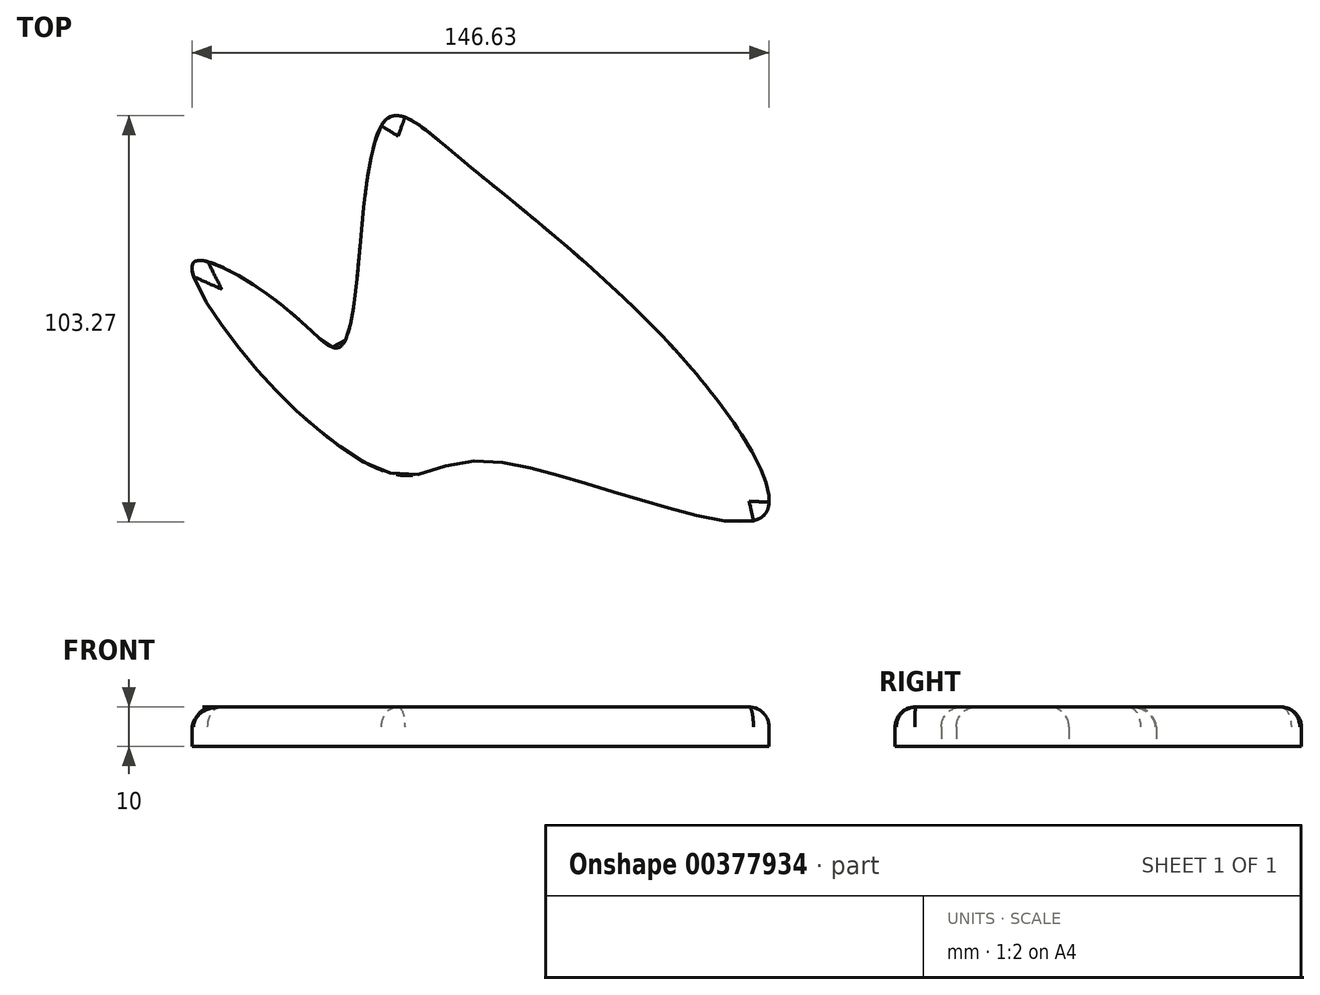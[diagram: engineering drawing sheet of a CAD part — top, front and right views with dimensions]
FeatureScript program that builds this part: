
annotation { "Feature Type Name" : "Feature", "Feature Type Description" : "" }
export const myFeature = defineFeature(function(context is Context, id is Id, definition is map)
    precondition{}
    {
        {
            var Q0;
            Q0=qCreatedBy(makeId("Top.planeOp"),FACE);
            var sketch = newSketch(context, id + "F0", { "sketchPlane" : qUnion([Q0])});
            skLineSegment(sketch, "E0", {"start": v(-136, -27.39) * mm, "end": v(-77.54, -6.3) * mm});
            skLineSegment(sketch, "E1", {"start": v(-118.9, 35.2) * mm, "end": v(-94.52, 0) * mm});
            skLineSegment(sketch, "E2", {"start": v(-77.54, -6.3) * mm, "end": v(-94.52, 0) * mm});
            skFitSpline(sketch, "E3", {"points": [v(126.55, -27.39) * mm, v(65.61, 27.87) * mm, v(47.85, 35.2) * mm, v(37.86, -20.84) * mm, v(25.14, -13.42) * mm, v(0, 0) * mm, v(15.93, -27.39) * mm, v(52.96, -54.3) * mm, v(74, -50.57) * mm, v(143.6, -65.21) * mm, v(126.55, -27.39) * mm]});
            skSolve(sketch);
        }
        {
            var Q0;
            Q0=makeQuery(id+"F0.imprint","IMPRINT",FACE,{"disambiguationData":[TD([[makeQuery(id+"F0.imprint","IMPRINT",EDGE,{"derivedFrom":sQuery(id+"F0.wireOp",EDGE,"E3")}),1.0]])]});
            extrude(context, id + "F1", {"entities" : qUnion([Q0]), "depth" : 10 * mm});
        }
        {
            var Q0;
            Q0=makeQuery(id+"F1.opExtrude","CAP_FACE",FACE,{"disambiguationData":[OSD([sQuery(id+"F0.wireOp",EDGE,"E3")])],"isStart":false});
            var Q1;
            Q1=makeQuery(id+"F1.opExtrude","CAP_EDGE",EDGE,{"disambiguationData":[OSD([sQuery(id+"F0.wireOp",EDGE,"E3")])],"isStart":false});
            fillet(context, id + "F2", {"entities" : qUnion([Q0, Q1]), "radius" : 5.08 * mm, "tangentPropagation" : true, "allowEdgeOverflow" : false});
        }
    });
